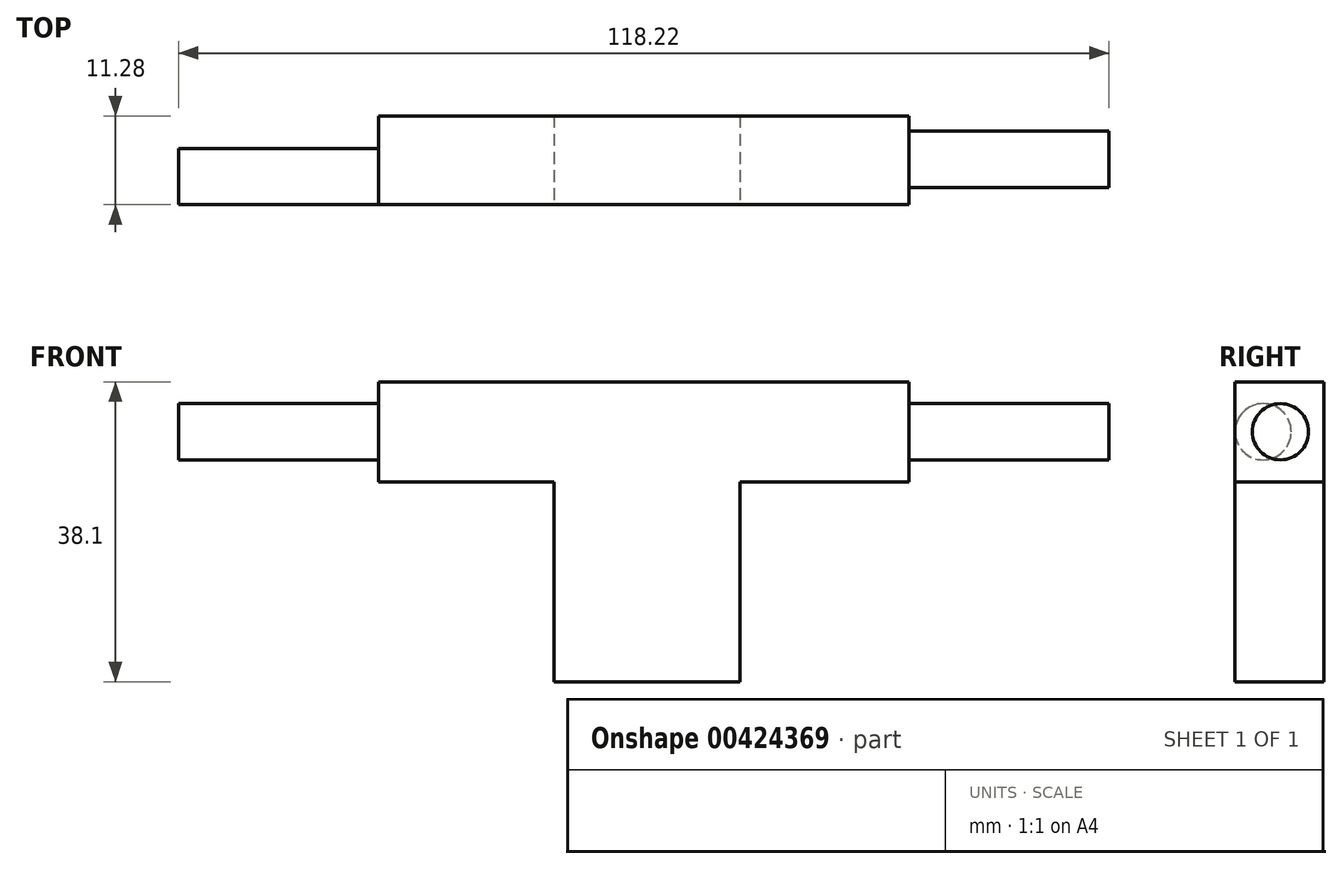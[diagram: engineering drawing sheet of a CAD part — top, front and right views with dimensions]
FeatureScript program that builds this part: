
annotation { "Feature Type Name" : "Feature", "Feature Type Description" : "" }
export const myFeature = defineFeature(function(context is Context, id is Id, definition is map)
    precondition{}
    {
        {
            var Q0;
            Q0=qCreatedBy(makeId("Top.planeOp"),FACE);
            var sketch = newSketch(context, id + "F0", { "sketchPlane" : qUnion([Q0])});
            skLineSegment(sketch, "E0.bottom", {"start": v(0, 0) * mm, "end": v(23.6, 0) * mm});
            skLineSegment(sketch, "E0.top", {"start": v(0, -11.28) * mm, "end": v(23.6, -11.28) * mm});
            skLineSegment(sketch, "E0.left", {"start": v(0, 0) * mm, "end": v(0, -11.28) * mm});
            skLineSegment(sketch, "E0.right", {"start": v(23.6, 0) * mm, "end": v(23.6, -11.28) * mm});
            skSolve(sketch);
        }
        {
            var Q0;
            Q0 = qSketchRegion(id + "F0", true);
            extrude(context, id + "F1", {"entities" : qUnion([Q0]), "depth" : 25.4 * mm});
        }
        {
            var Q0;
            Q0=makeQuery(id+"F1.opExtrude","CAP_FACE",FACE,{"disambiguationData":[OSD([sQuery(id+"F0.wireOp",EDGE,"E0.bottom"),sQuery(id+"F0.wireOp",EDGE,"E0.top"),sQuery(id+"F0.wireOp",EDGE,"E0.left"),sQuery(id+"F0.wireOp",EDGE,"E0.right")])],"isStart":false});
            var sketch = newSketch(context, id + "F2", { "sketchPlane" : qUnion([Q0])});
            skPoint(sketch, "E1.oppositeSnap0", {"position": v(11.8, -11.28) * mm});
            skLineSegment(sketch, "E1.bottom", {"start": v(-22.3, 0) * mm, "end": v(45.12, 0) * mm});
            skLineSegment(sketch, "E1.top", {"start": v(-22.3, -11.28) * mm, "end": v(45.12, -11.28) * mm});
            skLineSegment(sketch, "E1.left", {"start": v(-22.3, 0) * mm, "end": v(-22.3, -11.28) * mm});
            skLineSegment(sketch, "E1.right", {"start": v(45.12, 0) * mm, "end": v(45.12, -11.28) * mm});
            skSolve(sketch);
        }
        {
            var Q0;
            Q0 = qSketchRegion(id + "F2", true);
            extrude(context, id + "F3", {"entities" : qUnion([Q0]), "operationType" : NewBodyOperationType.ADD, "depth" : 12.7 * mm});
        }
        {
            var Q0;
            Q0=makeQuery(id+"F3.opExtrude","SWEPT_FACE",FACE,{"disambiguationData":[OSD([sQuery(id+"F2.wireOp",EDGE,"E1.right")])]});
            var sketch = newSketch(context, id + "F4", { "sketchPlane" : qUnion([Q0])});
            skCircle(sketch, "E2", {"center": v(-5.5, 31.75) * mm, "radius": 3.57 * mm});
            skPoint(sketch, "E2.centerSnap0", {"position": v(0, 31.75) * mm});
            skSolve(sketch);
        }
        {
            var Q0;
            Q0 = qSketchRegion(id + "F4", true);
            extrude(context, id + "F5", {"entities" : qUnion([Q0]), "operationType" : NewBodyOperationType.ADD, "depth" : 25.4 * mm});
        }
        {
            var Q0;
            Q0=makeQuery(id+"F3.opExtrude","SWEPT_FACE",FACE,{"disambiguationData":[OSD([sQuery(id+"F2.wireOp",EDGE,"E1.left")])]});
            var sketch = newSketch(context, id + "F6", { "sketchPlane" : qUnion([Q0])});
            skCircle(sketch, "E3", {"center": v(7.7, 31.75) * mm, "radius": 3.57 * mm});
            skPoint(sketch, "E3.centerSnap0", {"position": v(11.28, 31.75) * mm});
            skSolve(sketch);
        }
        {
            var Q0;
            Q0 = qSketchRegion(id + "F6", true);
            extrude(context, id + "F7", {"entities" : qUnion([Q0]), "operationType" : NewBodyOperationType.ADD, "depth" : 25.4 * mm});
        }
    });
